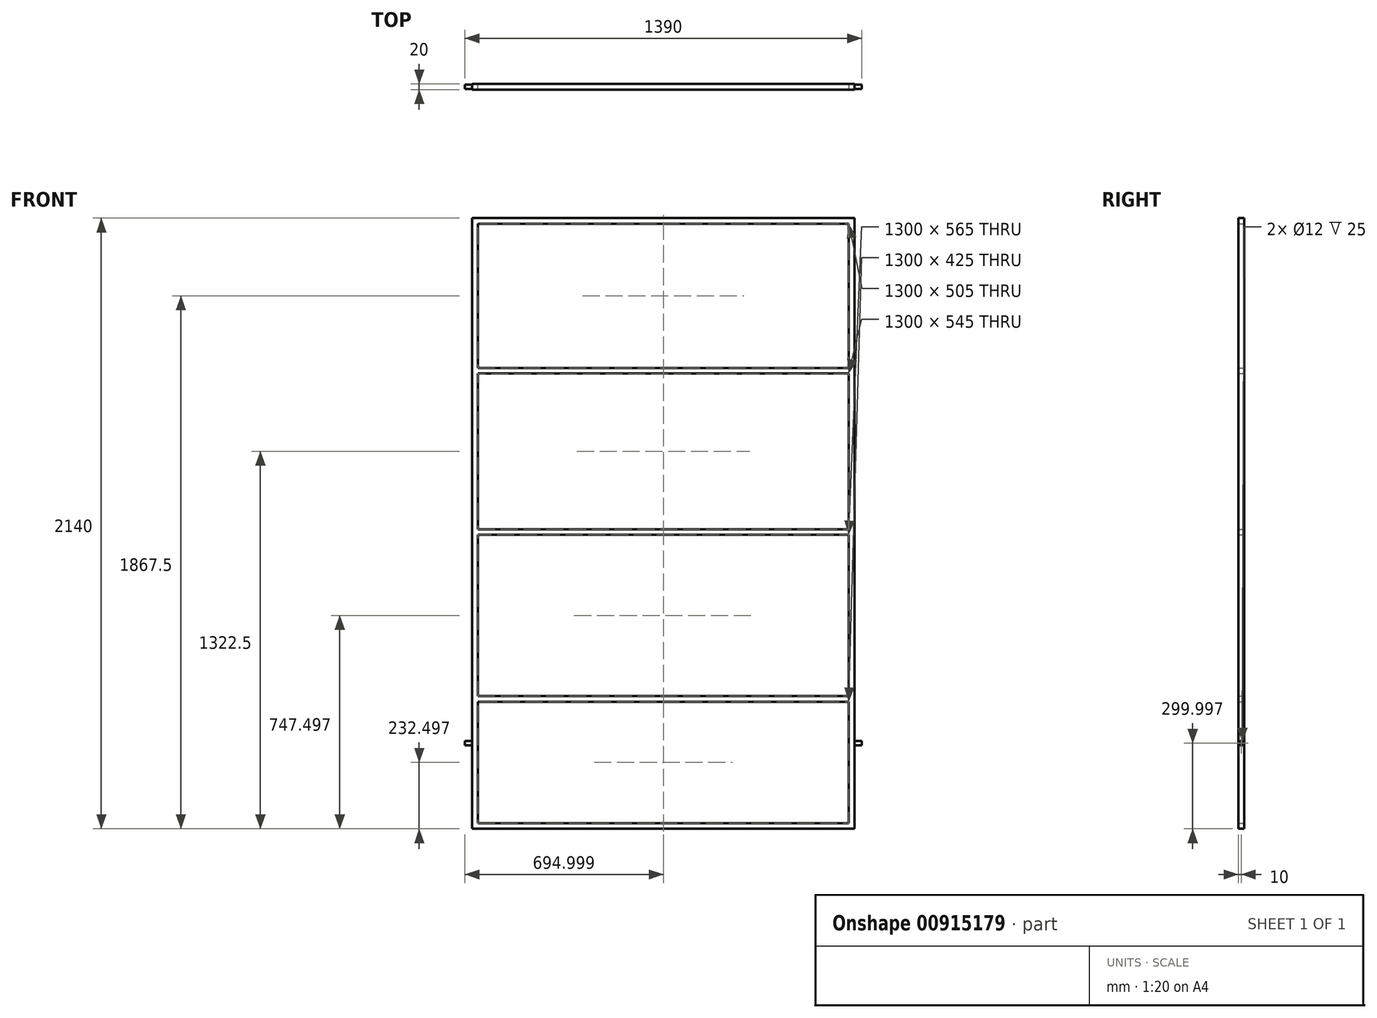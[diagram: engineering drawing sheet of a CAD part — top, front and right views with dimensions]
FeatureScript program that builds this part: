
annotation { "Feature Type Name" : "Feature", "Feature Type Description" : "" }
export const myFeature = defineFeature(function(context is Context, id is Id, definition is map)
    precondition{}
    {
        {
            var Q0;
            Q0=qCreatedBy(makeId("Front.planeOp"),FACE);
            var sketch = newSketch(context, id + "F0", { "sketchPlane" : qUnion([Q0])});
            skLineSegment(sketch, "E0.0", {"start": v(-686.82, 1037.88) * mm, "end": v(653.18, 1037.88) * mm});
            skLineSegment(sketch, "E1.0", {"start": v(633.18, 1057.88) * mm, "end": v(633.18, -1082.12) * mm});
            skLineSegment(sketch, "E2.0", {"start": v(-666.82, -1082.12) * mm, "end": v(-666.82, 1057.88) * mm});
            skLineSegment(sketch, "E3.0", {"start": v(653.18, -1062.12) * mm, "end": v(-686.82, -1062.12) * mm});
            skLineSegment(sketch, "E4.0", {"start": v(-686.82, 1057.88) * mm, "end": v(653.18, 1057.88) * mm});
            skLineSegment(sketch, "E5.0", {"start": v(653.18, 1057.88) * mm, "end": v(653.18, -1082.12) * mm});
            skLineSegment(sketch, "E6.0", {"start": v(653.18, -1082.12) * mm, "end": v(-686.82, -1082.12) * mm});
            skLineSegment(sketch, "E7.0", {"start": v(-686.82, -1082.12) * mm, "end": v(-686.82, 1057.88) * mm});
            skSolve(sketch);
        }
        {
            var Q0;
            Q0 = qSketchRegion(id + "F0", true);
            extrude(context, id + "F1", {"entities" : qUnion([Q0]), "depth" : 20 * mm, "offsetDistance" : 25 * mm});
        }
        {
            var Q0;
            Q0=qCreatedBy(makeId("Front.planeOp"),FACE);
            var sketch = newSketch(context, id + "F2", { "sketchPlane" : qUnion([Q0])});
            skLineSegment(sketch, "E8.0", {"start": v(-686.82, -32.12) * mm, "end": v(653.18, -32.12) * mm});
            skLineSegment(sketch, "E9.0", {"start": v(-686.82, -52.12) * mm, "end": v(653.18, -52.12) * mm});
            skLineSegment(sketch, "E10.0", {"start": v(-686.82, 512.88) * mm, "end": v(653.18, 512.88) * mm});
            skLineSegment(sketch, "E11.0", {"start": v(-686.82, 532.88) * mm, "end": v(653.18, 532.88) * mm});
            skLineSegment(sketch, "E12.MirrorCS", {"start": v(-686.82, -617.12) * mm, "end": v(653.18, -617.12) * mm});
            skLineSegment(sketch, "E13.MirrorCS", {"start": v(-686.82, -637.12) * mm, "end": v(653.18, -637.12) * mm});
            skLineSegment(sketch, "E14", {"start": v(-686.82, 532.88) * mm, "end": v(-686.82, -637.12) * mm});
            skLineSegment(sketch, "E15", {"start": v(653.18, -637.12) * mm, "end": v(653.18, 532.88) * mm});
            skSolve(sketch);
        }
        {
            var Q0;
            {var subQ0=sQuery(id+"F2.wireOp",EDGE,"E10.0");Q0=makeQuery(id+"F2.imprint","IMPRINT",FACE,{"disambiguationData":[TD([[makeQuery(id+"F2.imprint","IMPRINT",EDGE,{"derivedFrom":subQ0}),1.0]])]});}
            var Q1;
            {var subQ0=sQuery(id+"F2.wireOp",EDGE,"E8.0");Q1=makeQuery(id+"F2.imprint","IMPRINT",FACE,{"disambiguationData":[TD([[makeQuery(id+"F2.imprint","IMPRINT",EDGE,{"derivedFrom":subQ0}),-1.0]])]});}
            var Q2;
            {var subQ0=sQuery(id+"F2.wireOp",EDGE,"E12.MirrorCS");Q2=makeQuery(id+"F2.imprint","IMPRINT",FACE,{"disambiguationData":[TD([[makeQuery(id+"F2.imprint","IMPRINT",EDGE,{"derivedFrom":subQ0}),-1.0]])]});}
            extrude(context, id + "F3", {"entities" : qUnion([Q0, Q1, Q2]), "operationType" : NewBodyOperationType.ADD, "depth" : 20 * mm, "offsetDistance" : 25 * mm});
        }
        {
            var Q0;
            Q0=makeQuery(id+"F1.opExtrude","SWEPT_FACE",FACE,{"disambiguationData":[OSD([sQuery(id+"F0.wireOp",EDGE,"E7.0")])]});
            var sketch = newSketch(context, id + "F4", { "sketchPlane" : qUnion([Q0])});
            skLineSegment(sketch, "E16", {"start": v(10, -1082.12) * mm, "end": v(10, 1057.88) * mm, "construction": true});
            skLineSegment(sketch, "E17", {"start": v(10, -1082.12) * mm, "end": v(10, -782.12) * mm});
            skCircle(sketch, "E18", {"center": v(10, -782.12) * mm, "radius": 8 * mm});
            skCircle(sketch, "E19", {"center": v(10, -782.12) * mm, "radius": 6 * mm});
            skSolve(sketch);
        }
        {
            var Q0;
            Q0 = qSketchRegion(id + "F4", true);
            extrude(context, id + "F5", {"entities" : qUnion([Q0]), "operationType" : NewBodyOperationType.ADD, "depth" : 25 * mm, "offsetDistance" : 25 * mm});
        }
        {
            var Q0;
            Q0=makeQuery(id+"F1.opExtrude","SWEPT_FACE",FACE,{"disambiguationData":[OSD([sQuery(id+"F0.wireOp",EDGE,"E5.0")])]});
            var sketch = newSketch(context, id + "F6", { "sketchPlane" : qUnion([Q0])});
            skLineSegment(sketch, "E20", {"start": v(-10, -1082.12) * mm, "end": v(-10, 1219.11) * mm, "construction": true});
            skLineSegment(sketch, "E21", {"start": v(-10, -1082.12) * mm, "end": v(-10, -782.12) * mm});
            skCircle(sketch, "E22", {"center": v(-10, -782.12) * mm, "radius": 8 * mm});
            skCircle(sketch, "E23", {"center": v(-10, -782.12) * mm, "radius": 6 * mm});
            skSolve(sketch);
        }
        {
            var Q0;
            Q0 = qSketchRegion(id + "F6", true);
            extrude(context, id + "F7", {"entities" : qUnion([Q0]), "operationType" : NewBodyOperationType.ADD, "depth" : 25 * mm, "offsetDistance" : 25 * mm});
        }
    });
